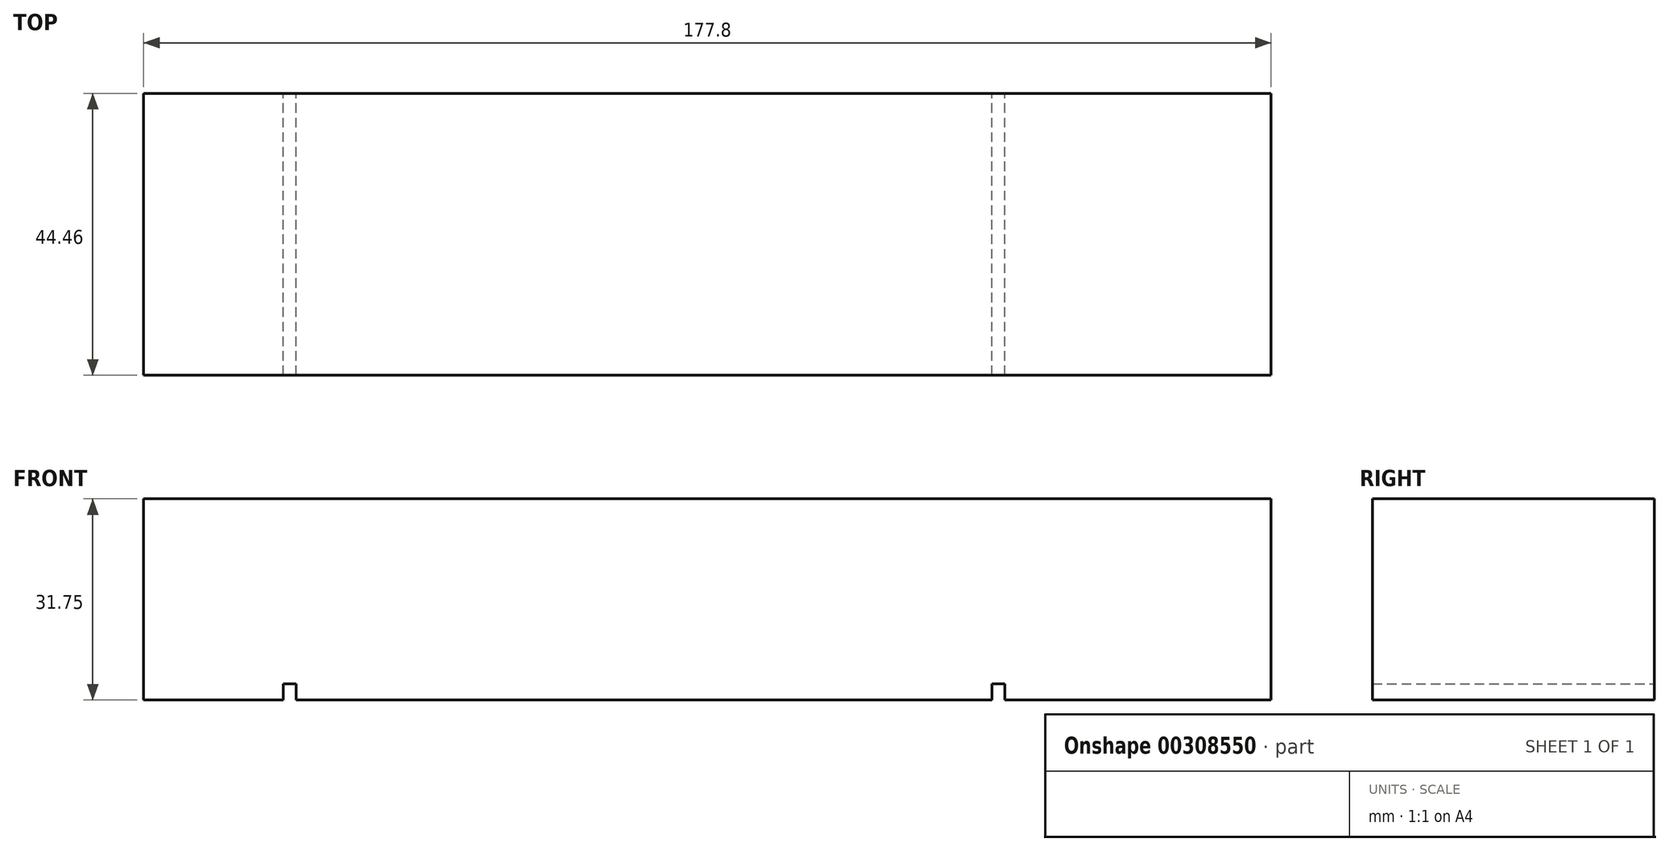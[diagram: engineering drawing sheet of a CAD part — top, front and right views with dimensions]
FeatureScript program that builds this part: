
annotation { "Feature Type Name" : "Feature", "Feature Type Description" : "" }
export const myFeature = defineFeature(function(context is Context, id is Id, definition is map)
    precondition{}
    {
        {
            var Q0;
            Q0=qCreatedBy(makeId("Top.planeOp"),FACE);
            var sketch = newSketch(context, id + "F0", { "sketchPlane" : qUnion([Q0])});
            skLineSegment(sketch, "E0.bottom", {"start": v(88.9, -22.22) * mm, "end": v(-88.9, -22.23) * mm});
            skLineSegment(sketch, "E0.top", {"start": v(88.9, 22.23) * mm, "end": v(-88.9, 22.22) * mm});
            skLineSegment(sketch, "E0.left", {"start": v(88.9, -22.22) * mm, "end": v(88.9, 22.23) * mm});
            skLineSegment(sketch, "E0.right", {"start": v(-88.9, -22.23) * mm, "end": v(-88.9, 22.22) * mm});
            skPoint(sketch, "E0.middle", {"position": v(0, 0) * mm});
            skSolve(sketch);
        }
        {
            var Q0;
            Q0=makeQuery(id+"F0.imprint","IMPRINT",FACE,{"disambiguationData":[TD([[makeQuery(id+"F0.imprint","IMPRINT",EDGE,{"derivedFrom":sQuery(id+"F0.wireOp",EDGE,"E0.bottom")}),-1.0]])]});
            extrude(context, id + "F1", {"entities" : qUnion([Q0]), "depth" : 31.75 * mm});
        }
        {
            var Q0;
            Q0=qCreatedBy(makeId("Front.planeOp"),FACE);
            var sketch = newSketch(context, id + "F2", { "sketchPlane" : qUnion([Q0])});
            skLineSegment(sketch, "E1.bottom", {"start": v(-64.87, 2.54) * mm, "end": v(-66.9, 2.54) * mm});
            skLineSegment(sketch, "E1.top", {"start": v(-64.87, -2.54) * mm, "end": v(-66.9, -2.54) * mm});
            skLineSegment(sketch, "E1.left", {"start": v(-64.87, 2.54) * mm, "end": v(-64.87, -2.54) * mm});
            skLineSegment(sketch, "E1.right", {"start": v(-66.9, 2.54) * mm, "end": v(-66.9, -2.54) * mm});
            skPoint(sketch, "E1.middle", {"position": v(-65.89, 0) * mm});
            skLineSegment(sketch, "E2.bottom", {"start": v(46.89, 2.54) * mm, "end": v(44.86, 2.54) * mm});
            skLineSegment(sketch, "E2.top", {"start": v(46.89, -0.42) * mm, "end": v(44.86, -0.42) * mm});
            skLineSegment(sketch, "E2.left", {"start": v(46.89, 2.54) * mm, "end": v(46.89, -0.42) * mm});
            skLineSegment(sketch, "E2.right", {"start": v(44.86, 2.54) * mm, "end": v(44.86, -0.42) * mm});
            skPoint(sketch, "E2.middle", {"position": v(45.87, 1.06) * mm});
            skSolve(sketch);
        }
        {
            var Q0;
            Q0=makeQuery(id+"F2.imprint","IMPRINT",FACE,{"disambiguationData":[TD([[makeQuery(id+"F2.imprint","IMPRINT",EDGE,{"derivedFrom":sQuery(id+"F2.wireOp",EDGE,"E1.bottom")}),1.0]])]});
            var Q1;
            Q1=makeQuery(id+"F2.imprint","IMPRINT",FACE,{"disambiguationData":[TD([[makeQuery(id+"F2.imprint","IMPRINT",EDGE,{"derivedFrom":sQuery(id+"F2.wireOp",EDGE,"E2.bottom")}),1.0]])]});
            extrude(context, id + "F3", {"entities" : qUnion([Q0, Q1]), "operationType" : NewBodyOperationType.REMOVE, "depth" : 141.73 * mm, "symmetric" : true});
        }
    });
